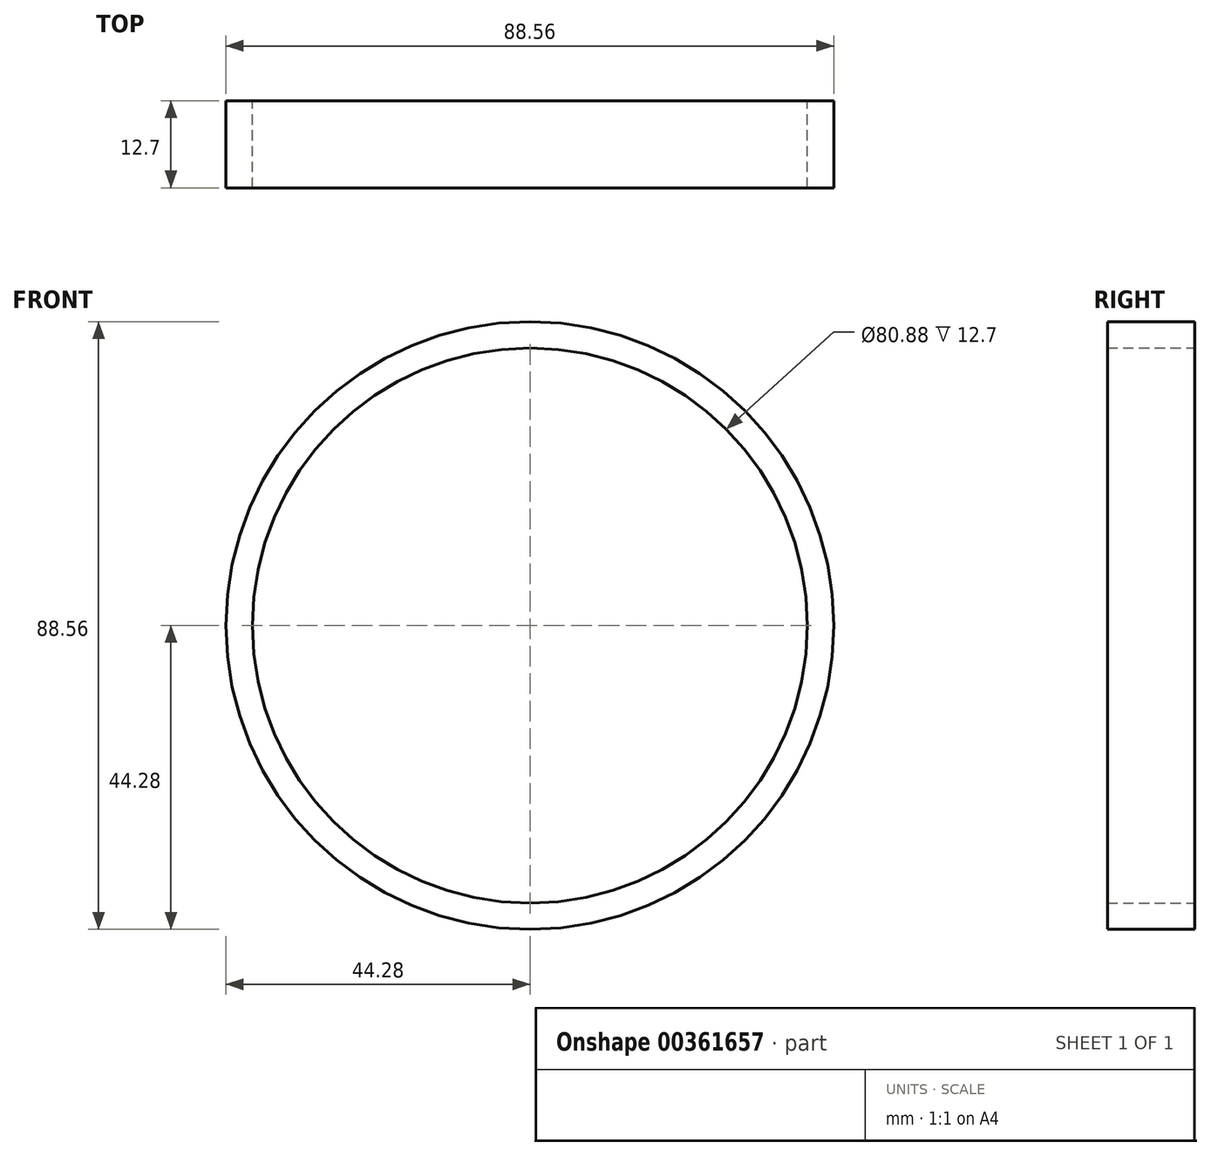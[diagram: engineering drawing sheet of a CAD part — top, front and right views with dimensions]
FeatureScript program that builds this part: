
annotation { "Feature Type Name" : "Feature", "Feature Type Description" : "" }
export const myFeature = defineFeature(function(context is Context, id is Id, definition is map)
    precondition{}
    {
        {
            var Q0;
            Q0=qCreatedBy(makeId("Front.planeOp"),FACE);
            var sketch = newSketch(context, id + "F0", { "sketchPlane" : qUnion([Q0])});
            skCircle(sketch, "E0", {"center": v(0, 0) * mm, "radius": 44.28 * mm});
            skCircle(sketch, "E1", {"center": v(0, 0) * mm, "radius": 40.44 * mm});
            skFitSpline(sketch, "E2", {"points": [v(-40.44, 0) * mm, v(-17.7, 17.89) * mm, v(0, 0) * mm, v(19.86, -16.12) * mm, v(40.44, 0) * mm], "startDerivative": vector(91.5, 105.77) * mm, "endDerivative": vector(82.5, 96.93) * mm});
            skArc(sketch, "E3", {"start": v(23.6, 11.8) * mm, "mid": v(14.37, 30.74) * mm, "end": v(0, 15.33) * mm});
            skArc(sketch, "E4.MirrorCS", {"start": v(23.6, -11.8) * mm, "mid": v(24.3, -13.26) * mm, "end": v(24.82, -14.8) * mm});
            skArc(sketch, "E5.MirrorCS", {"start": v(-23.6, -11.8) * mm, "mid": v(-14.37, -30.74) * mm, "end": v(0, -15.33) * mm});
            skPoint(sketch, "E6.trimOffspring.end.orphan", {"position": v(0, -15.33) * mm});
            skSolve(sketch);
        }
        {
            var Q0;
            Q0 = qSketchRegion(id + "F0", true);
            extrude(context, id + "F1", {"entities" : qUnion([Q0]), "endBound" : BoundingType.SYMMETRIC, "depth" : 12.7 * mm});
        }
        {
            var Q0;
            Q0=sQuery(id+"F0.wireOp",EDGE,"E2");
            extrude(context, id + "F2", {"bodyType" : ToolBodyType.SURFACE, "surfaceEntities" : qUnion([Q0]), "endBound" : BoundingType.SYMMETRIC, "depth" : 12.7 * mm});
        }
        {
            var Q0;
            Q0=makeQuery(id+"F1.opExtrude","CAP_FACE",FACE,{"disambiguationData":[OSD([sQuery(id+"F0.wireOp",EDGE,"E0"),sQuery(id+"F0.wireOp",EDGE,"E1")])],"isStart":false});
            var sketch = newSketch(context, id + "F3", { "sketchPlane" : qUnion([Q0])});
            skFitSpline(sketch, "E7", {"points": [v(44.28, 0) * mm, v(67.78, 0) * mm, v(64.9, -3.4) * mm, v(60.62, 0) * mm], "startDerivative": vector(65.6, 7.84) * mm, "endDerivative": vector(-15.8, 21.86) * mm});
            skSolve(sketch);
        }
        {
            var Q0;
            Q0=sQuery(id+"F3.wireOp",EDGE,"E7");
            extrude(context, id + "F4", {"bodyType" : ToolBodyType.SURFACE, "surfaceEntities" : qUnion([Q0]), "oppositeDirection" : true, "depth" : 1.27 * mm});
        }
    });
